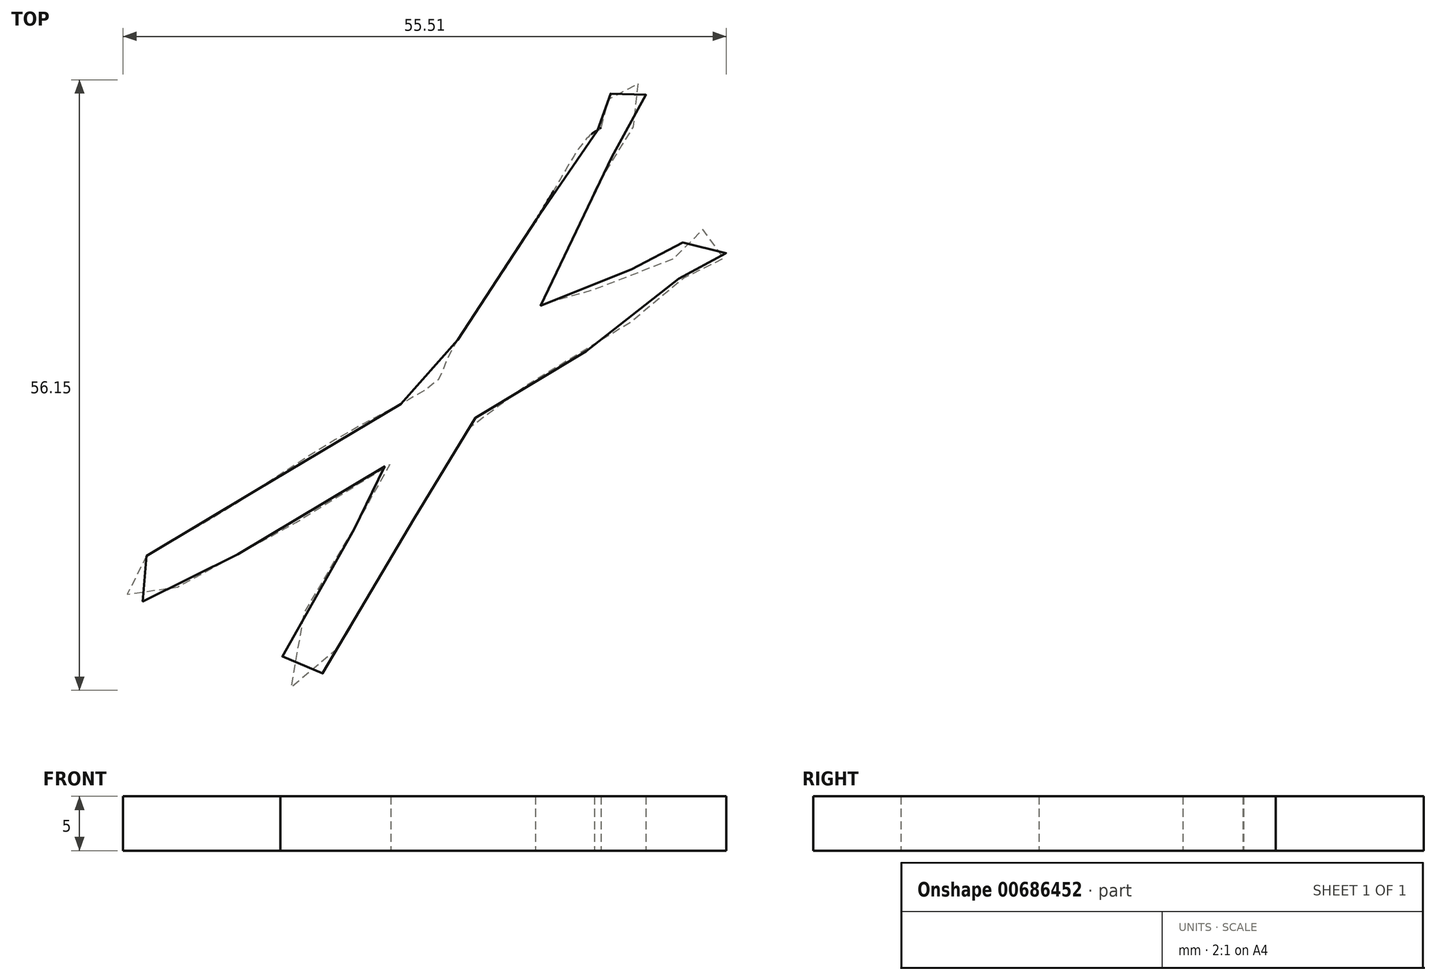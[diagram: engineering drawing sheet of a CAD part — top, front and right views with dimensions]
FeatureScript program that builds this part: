
annotation { "Feature Type Name" : "Feature", "Feature Type Description" : "" }
export const myFeature = defineFeature(function(context is Context, id is Id, definition is map)
    precondition{}
    {
        {
            var Q0;
            Q0=qCreatedBy(makeId("Top.planeOp"),FACE);
            var sketch = newSketch(context, id + "F0", { "sketchPlane" : qUnion([Q0])});
            skFitSpline(sketch, "E0", {"points": [v(-60.13, 18.34) * mm, v(-61.85, 16.61) * mm, v(-62.2, 15.16) * mm, v(-59.78, 14.06) * mm, v(-57.99, 15.03) * mm, v(-44.58, 22.49) * mm, v(-37.68, 26.7) * mm, v(-39.54, 23.6) * mm, v(-42.37, 18.34) * mm, v(-47.83, 8.05) * mm, v(-46.66, 6.18) * mm, v(-45.14, 6.25) * mm, v(-38.64, 16.68) * mm, v(-30.84, 29.32) * mm, v(-29.94, 30.98) * mm, v(-24.48, 34.44) * mm, v(-13.91, 41.2) * mm, v(-11.15, 43.83) * mm, v(-10.2, 43.95) * mm, v(-8.1, 45.01) * mm, v(-6.9, 45.92) * mm, v(-7.17, 47.9) * mm, v(-8.56, 48.48) * mm, v(-10.88, 47.09) * mm, v(-11.58, 46.28) * mm, v(-11.7, 45.58) * mm, v(-13.56, 45.46) * mm, v(-24.13, 40) * mm, v(-23.43, 42.2) * mm, v(-17.16, 55.34) * mm, v(-16.11, 56.73) * mm, v(-14.37, 59.75) * mm, v(-14.37, 61.5) * mm, v(-15.18, 61.84) * mm, v(-16.7, 62.08) * mm, v(-17.5, 60.68) * mm, v(-18.2, 59.52) * mm, v(-18.9, 58.24) * mm, v(-18.32, 57.78) * mm, v(-19.13, 57.2) * mm, v(-22.39, 52.43) * mm, v(-28.08, 43.37) * mm, v(-32.6, 36.17) * mm, v(-33.3, 34.54) * mm, v(-41.67, 29.66) * mm, v(-53.99, 21.88) * mm, v(-60.13, 18.34) * mm]});
            skSolve(sketch);
        }
        {
            var Q0;
            Q0 = qSketchRegion(id + "F0", true);
            extrude(context, id + "F1", {"entities" : qUnion([Q0]), "depth" : 5 * mm, "offsetDistance" : 25.4 * mm});
        }
    });
